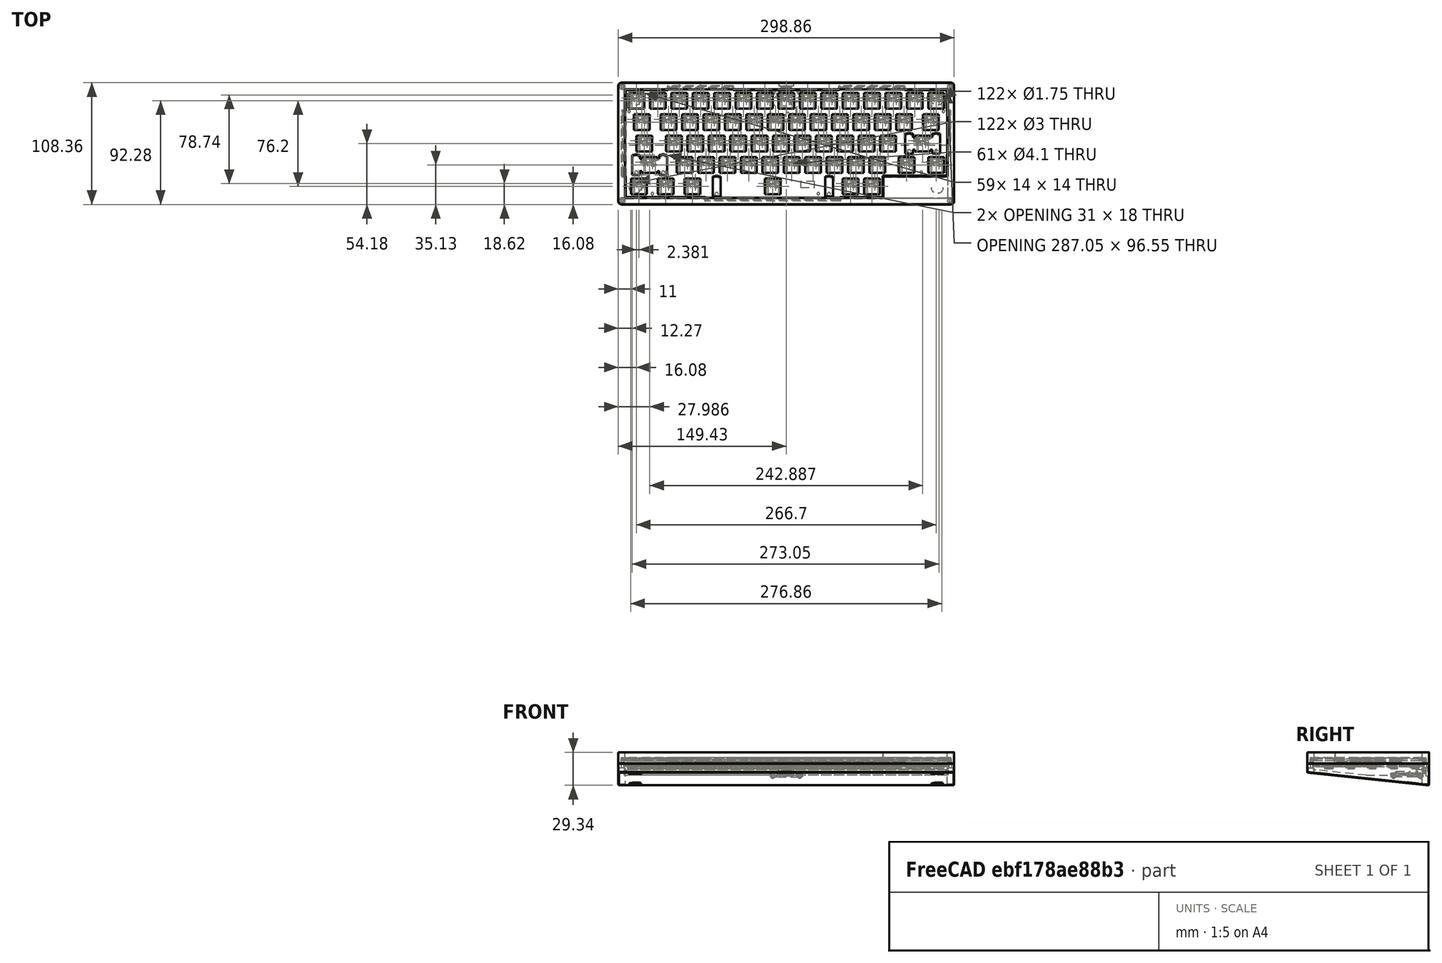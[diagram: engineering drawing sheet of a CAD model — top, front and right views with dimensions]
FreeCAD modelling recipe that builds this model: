
FCSTD DOCUMENT  (FreeCAD 0.20R29603 (Git))
Label: Five_Octave_Enclosure_v2
License: All rights reserved
LicenseURL: http://en.wikipedia.org/wiki/All_rights_reserved
objects: Sketcher::SketchObject×17, PartDesign::Pocket×9, TechDraw::DrawViewBalloon×8, PartDesign::Fillet×6, PartDesign::Pad×5, PartDesign::Body×4, Part::Feature×3, PartDesign::Hole×3, PartDesign::Chamfer×3, TechDraw::DrawSVGTemplate×2, TechDraw::DrawProjGroupItem×2, TechDraw::DrawProjGroup×2, TechDraw::DrawPage×2, Part::MultiFuse×1, App::DocumentObjectGroup×1, PartDesign::Boolean×1
note: 78 computed .brp shape members not serialized (recipe doc carries the construction recipe); baked Part::Feature solids carry a one-line shape summary decoded from their .brp

FEATURE [Part::Feature] Feature001  label="Five_Octave_Keys"
  Placement = pos=(0,0,-4.2) rot=(0,1,0;3.14159rad)
  shape: bbox 285.8 x 95.25 x 3.65 mm, 9961 faces, 246 solids (baked)
  expr: .Placement.Base.z = -0.8mm - 3.4mm
FEATURE [Part::Feature] Solid  label="Five_Octave_Plate"
  Placement = pos=(0,0,-0.8) rot=(0,0,1;0rad)
  shape: bbox 290.8 x 100.3 x 1.6 mm, 520 faces (baked)
FEATURE [Part::Feature] Feature  label="Five_Octave_MCU"
  shape: bbox 28.58 x 28.58 x 3.65 mm, 932 faces, 28 solids (baked)
FEATURE [Sketcher::SketchObject] Sketch
  AttachmentOffset = pos=(0,0,1.65) rot=(0,0,1;0rad)
  FullyConstrained = true
  MapMode = 5
  Placement = pos=(0,0,1.65) rot=(0,0,1;0rad)
  Support = -> [XY_Plane]
  expr: Constraints[12] = 15.637mm
  sketch-geometry (5):
    g0: LineSegment StartX=-4.47 StartY=15.637 StartZ=0 EndX=4.47 EndY=15.637 EndZ=0
    g1: LineSegment StartX=4.47 StartY=15.637 StartZ=0 EndX=4.47 EndY=8.337 EndZ=0
    g2: LineSegment StartX=4.47 StartY=8.337 StartZ=0 EndX=-4.47 EndY=8.337 EndZ=0
    g3: LineSegment StartX=-4.47 StartY=8.337 StartZ=0 EndX=-4.47 EndY=15.637 EndZ=0
    g4: GeomPoint X=0 Y=15.637 Z=0
  constraints (13):
    c: Coincident(g0,g1)
    c: Coincident(g1,g2)
    c: Coincident(g2,g3)
    c: Coincident(g3,g0)
    c: Horizontal(g0)
    c: Horizontal(g2)
    c: Vertical(g1)
    c: Vertical(g3)
    c: DistanceX(g0,g0) = 8.94
    c: DistanceY(g1,g1) = 7.3
    c: Symmetric(g0,g0,g4)
    c: PointOnObject(g4,g-2)
    c: DistanceY(g-1,g4) = 15.637
FEATURE [PartDesign::Pad] Pad
  Direction = (0,0,1)
  Length = 3.2
  Length2 = 10
  Profile = -> Sketch
  ReferenceAxis = -> Sketch [N_Axis]
  Type = 0
FEATURE [Sketcher::SketchObject] Sketch001
  ExternalGeometry = -> [Pad]
  FullyConstrained = true
  MapMode = 5
  Placement = pos=(0,15.637,0) rot=(0,0.707107,0.707107;3.14159rad)
  Support = -> [Pad]
  sketch-geometry (12):
    g0: ArcOfCircle CenterX=-3.22 CenterY=3.6 CenterZ=0 NormalX=0 NormalY=0 NormalZ=1 AngleXU=0 Radius=1.25 StartAngle=1.5708 EndAngle=3.14159
    g1: LineSegment StartX=-4.47 StartY=4.85 StartZ=0 EndX=-3.22 EndY=4.85 EndZ=0
    g2: LineSegment StartX=-4.47 StartY=3.6 StartZ=0 EndX=-4.47 EndY=4.85 EndZ=0
    g3: ArcOfCircle CenterX=3.22 CenterY=3.6 CenterZ=0 NormalX=0 NormalY=0 NormalZ=1 AngleXU=0 Radius=1.25 StartAngle=1e-16 EndAngle=1.5708
    g4: LineSegment StartX=3.22 StartY=4.85 StartZ=0 EndX=4.47 EndY=4.85 EndZ=0
    g5: LineSegment StartX=4.47 StartY=3.6 StartZ=0 EndX=4.47 EndY=4.85 EndZ=0
    g6: ArcOfCircle CenterX=-3.22 CenterY=2.9 CenterZ=0 NormalX=0 NormalY=0 NormalZ=1 AngleXU=0 Radius=1.25 StartAngle=3.14159 EndAngle=4.71239
    g7: LineSegment StartX=-4.47 StartY=1.65 StartZ=0 EndX=-4.47 EndY=2.9 EndZ=0
    g8: LineSegment StartX=-4.47 StartY=1.65 StartZ=0 EndX=-3.22 EndY=1.65 EndZ=0
    g9: ArcOfCircle CenterX=3.22 CenterY=2.9 CenterZ=0 NormalX=0 NormalY=0 NormalZ=1 AngleXU=0 Radius=1.25 StartAngle=4.71239 EndAngle=6.28319
    g10: LineSegment StartX=4.47 StartY=1.65 StartZ=0 EndX=3.22 EndY=1.65 EndZ=0
    g11: LineSegment StartX=4.47 StartY=1.65 StartZ=0 EndX=4.47 EndY=2.9 EndZ=0
  constraints (36):
    c: PointOnObject(g0,g-3)
    c: PointOnObject(g0,g-5)
    c: Radius(g0) = 1.25
    c: Coincident(g1,g-5)
    c: Coincident(g1,g0)
    c: DistanceX(g1,g1) = 1.25
    c: Coincident(g2,g0)
    c: Coincident(g2,g1)
    c: DistanceY(g2,g2) = 1.25
    c: PointOnObject(g3,g-3)
    c: PointOnObject(g3,g-6)
    c: Coincident(g4,g3)
    c: Coincident(g4,g-6)
    c: Coincident(g5,g4)
    c: Coincident(g5,g3)
    c: PointOnObject(g6,g-5)
    c: PointOnObject(g6,g-4)
    c: Equal(g6,g0)
    c: Equal(g3,g0)
    c: Equal(g1,g4)
    c: Equal(g5,g2)
    c: Coincident(g7,g-5)
    c: Coincident(g8,g7)
    c: Coincident(g8,g6)
    c: Coincident(g6,g7)
    c: Equal(g7,g2)
    c: Equal(g1,g8)
    c: PointOnObject(g9,g-6)
    c: PointOnObject(g9,g-4)
    c: Equal(g9,g0)
    c: Coincident(g10,g-6)
    c: Coincident(g11,g10)
    c: Coincident(g9,g11)
    c: Coincident(g10,g9)
    c: Equal(g10,g1)
    c: Equal(g11,g2)
FEATURE [PartDesign::Pocket] Pocket
  BaseFeature = -> Pad
  Direction = (0,-1,2e-16)
  Length = 7.3
  Length2 = 5
  Profile = -> Sketch001
  ReferenceAxis = -> Sketch001 [N_Axis]
  Type = 0
FEATURE [PartDesign::Body] Body  label="USB"
  Group = -> [Sketch,Pad,Sketch001,Pocket]
  Origin = -> Origin
  Tip = -> Pocket
FEATURE [Part::MultiFuse] Fusion  label="MCU"
  Placement = pos=(0,34.3875,-13.6) rot=(-1,0,0;0rad)
  Shapes = -> [Body,Feature]
  expr: .Placement.Base.y = 19.05mm * 2.5 - 28.575mm / 2 + 1.05mm
  expr: .Placement.Base.z = -0.8mm - 5mm - 7.8mm
FEATURE [App::DocumentObjectGroup] Group  label="External Components"
  Group = -> [Solid,Feature001,Fusion]
FEATURE [Sketcher::SketchObject] Sketch002
  AttachmentOffset = pos=(0,0,-3.2) rot=(0,0,1;0rad)
  FullyConstrained = true
  MapMode = 5
  Placement = pos=(0,0,-3.2) rot=(0,0,1;0rad)
  Support = -> [XY_Plane001]
  expr: .AttachmentOffset.Base.z = -2mm - 1.2mm
  expr: Constraints[10] = 19.05mm * 15 + (0.55mm + 6mm) * 2
  expr: Constraints[11] = 19.05mm * 5 + (0.55mm + 6mm) * 2
  sketch-geometry (5):
    g0: LineSegment StartX=149.425 StartY=-54.175 StartZ=0 EndX=149.425 EndY=54.175 EndZ=0
    g1: LineSegment StartX=149.425 StartY=54.175 StartZ=0 EndX=-149.425 EndY=54.175 EndZ=0
    g2: LineSegment StartX=-149.425 StartY=54.175 StartZ=0 EndX=-149.425 EndY=-54.175 EndZ=0
    g3: LineSegment StartX=-149.425 StartY=-54.175 StartZ=0 EndX=149.425 EndY=-54.175 EndZ=0
    g4: GeomPoint X=0 Y=0 Z=0
  constraints (12):
    c: Coincident(g0,g1)
    c: Coincident(g1,g2)
    c: Coincident(g2,g3)
    c: Coincident(g3,g0)
    c: Horizontal(g1)
    c: Horizontal(g3)
    c: Vertical(g0)
    c: Vertical(g2)
    c: Symmetric(g1,g0,g4)
    c: Coincident(g4,g-1)
    c: DistanceX(g1,g1) = 298.85
    c: DistanceY(g2,g2) = 108.35
FEATURE [PartDesign::Pad] Pad001  label="Pad001 - Base"
  Direction = (0,0,-1)
  Length = 20
  Length2 = 10
  Profile = -> Sketch002
  ReferenceAxis = -> Sketch002 [N_Axis]
  Type = 0
  UseCustomVector = true
FEATURE [Sketcher::SketchObject] Sketch003
  ExternalGeometry = -> [Pad001]
  FullyConstrained = true
  MapMode = 5
  Placement = pos=(149.425,0,0) rot=(0.57735,0.57735,0.57735;2.0944rad)
  Support = -> [Pad001]
  sketch-geometry (6):
    g0: LineSegment StartX=-54.175 StartY=-11.2 StartZ=0 EndX=54.175 EndY=-22.588 EndZ=0
    g1: LineSegment StartX=54.175 StartY=-22.588 StartZ=0 EndX=54.175 EndY=-23.2 EndZ=0
    g2: LineSegment StartX=54.175 StartY=-23.2 StartZ=0 EndX=-54.175 EndY=-23.2 EndZ=0
    g3: LineSegment StartX=-54.175 StartY=-23.2 StartZ=0 EndX=-54.175 EndY=-11.2 EndZ=0
    g4: LineSegment StartX=-54.175 StartY=-7.17797 StartZ=0 EndX=54.175 EndY=-18.566 EndZ=0
    g5: LineSegment StartX=-54.175 StartY=-11.2 StartZ=0 EndX=-53.7569 EndY=-7.22191 EndZ=0
  constraints (18):
    c: PointOnObject(g0,g-3)
    c: PointOnObject(g0,g-4)
    c: Coincident(g1,g0)
    c: Coincident(g1,g-4)
    c: Coincident(g2,g1)
    c: Coincident(g2,g-3)
    c: Coincident(g3,g2)
    c: Coincident(g3,g0)
    c: DistanceY(g0,g-4) = 19.388
    c: PointOnObject(g4,g-4)
    c: PointOnObject(g4,g-3)
    c: Angle(g0,g-1) = 0.10472
    c: Equal(g0,g4)
    c: Coincident(g5,g0)
    c: PointOnObject(g5,g4)
    c: Perpendicular(g5,g4)
    c: Distance(g5) = 4
    c: DistanceY(g0,g-3) = 8
FEATURE [PartDesign::Pocket] Pocket001  label="Pocket001 - Base angle"
  BaseFeature = -> Pad001
  Direction = (-1,0,0)
  Length = 300
  Length2 = 5
  Profile = -> Sketch003
  ReferenceAxis = -> Sketch003 [N_Axis]
  Type = 0
FEATURE [Sketcher::SketchObject] Sketch004
  FullyConstrained = true
  MapMode = 5
  Support = -> [XY_Plane002]
  expr: Constraints[10] = 19.05mm * 15 + (0.55mm + 6mm) * 2
  expr: Constraints[11] = 19.05mm * 5 + (0.55mm + 6mm) * 2
  expr: Constraints[29] = 19.05mm * 3
  sketch-geometry (11):
    g0: LineSegment StartX=149.425 StartY=-54.175 StartZ=0 EndX=149.425 EndY=54.175 EndZ=0
    g1: LineSegment StartX=149.425 StartY=54.175 StartZ=0 EndX=-149.425 EndY=54.175 EndZ=0
    g2: LineSegment StartX=-149.425 StartY=54.175 StartZ=0 EndX=-149.425 EndY=-54.175 EndZ=0
    g3: LineSegment StartX=-149.425 StartY=-54.175 StartZ=0 EndX=149.425 EndY=-54.175 EndZ=0
    g4: GeomPoint X=0 Y=0 Z=0
    g5: LineSegment StartX=-143.425 StartY=48.175 StartZ=0 EndX=-143.425 EndY=-48.175 EndZ=0
    g6: LineSegment StartX=-143.425 StartY=-48.175 StartZ=0 EndX=86.275 EndY=-48.175 EndZ=0
    g7: LineSegment StartX=86.275 StartY=-48.175 StartZ=0 EndX=86.275 EndY=-29.125 EndZ=0
    g8: LineSegment StartX=86.275 StartY=-29.125 StartZ=0 EndX=143.425 EndY=-29.125 EndZ=0
    g9: LineSegment StartX=143.425 StartY=-29.125 StartZ=0 EndX=143.425 EndY=48.175 EndZ=0
    g10: LineSegment StartX=143.425 StartY=48.175 StartZ=0 EndX=-143.425 EndY=48.175 EndZ=0
  constraints (32):
    c: Coincident(g0,g1)
    c: Coincident(g1,g2)
    c: Coincident(g2,g3)
    c: Coincident(g3,g0)
    c: Horizontal(g1)
    c: Horizontal(g3)
    c: Vertical(g0)
    c: Vertical(g2)
    c: Symmetric(g1,g0,g4)
    c: Coincident(g4,g-1)
    c: DistanceX(g1,g1) = 298.85
    c: DistanceY(g2,g2) = 108.35
    c: Vertical(g5)
    c: Coincident(g6,g5)
    c: Horizontal(g6)
    c: Coincident(g7,g6)
    c: Vertical(g7)
    c: Coincident(g8,g7)
    c: Horizontal(g8)
    c: Coincident(g9,g8)
    c: Vertical(g9)
    c: Coincident(g10,g9)
    c: Coincident(g10,g5)
    c: Horizontal(g10)
    c: DistanceY(g5,g1) = 6
    c: DistanceX(g9,g0) = 6
    c: DistanceX(g1,g5) = 6
    c: DistanceY(g2,g5) = 6
    c: DistanceY(g7,g7) = 19.05
    c: DistanceX(g8,g8) = 57.15
    c: DistanceX(g10,g10) = 286.85
    c: DistanceY(g5,g5) = 96.35
FEATURE [PartDesign::Pad] Pad002
  Direction = (0,0,1)
  Length = 6.8
  Length2 = 3.2
  Profile = -> Sketch004
  ReferenceAxis = -> Sketch004 [N_Axis]
  Type = 4
  expr: Length = 0.8mm + 6mm
FEATURE [Sketcher::SketchObject] Sketch006
  AttachmentOffset = pos=(0,0,-3.2) rot=(0,0,1;0rad)
  FullyConstrained = true
  MapMode = 5
  Placement = pos=(0,0,-3.2) rot=(0,0,1;0rad)
  Support = -> [XY_Plane003]
  expr: Constraints[10] = 19.05mm * 15 + 1mm * 2 + 0.05mm * 2
  expr: Constraints[11] = 19.05mm * 5 + 1mm * 2 + 0.05mm * 2
  sketch-geometry (5):
    g0: LineSegment StartX=-143.925 StartY=48.675 StartZ=0 EndX=-143.925 EndY=-48.675 EndZ=0
    g1: LineSegment StartX=-143.925 StartY=-48.675 StartZ=0 EndX=143.925 EndY=-48.675 EndZ=0
    g2: LineSegment StartX=143.925 StartY=-48.675 StartZ=0 EndX=143.925 EndY=48.675 EndZ=0
    g3: LineSegment StartX=143.925 StartY=48.675 StartZ=0 EndX=-143.925 EndY=48.675 EndZ=0
    g4: GeomPoint X=0 Y=0 Z=0
  constraints (12):
    c: Coincident(g0,g1)
    c: Coincident(g1,g2)
    c: Coincident(g2,g3)
    c: Coincident(g3,g0)
    c: Horizontal(g1)
    c: Horizontal(g3)
    c: Vertical(g0)
    c: Vertical(g2)
    c: Symmetric(g1,g0,g4)
    c: Coincident(g4,g-1)
    c: DistanceX(g3,g3) = 287.85
    c: DistanceY(g0,g0) = 97.35
FEATURE [PartDesign::Pad] Pad003
  Direction = (0,0,-1)
  Length = 20
  Length2 = 10
  Profile = -> Sketch006
  ReferenceAxis = -> Sketch006 [N_Axis]
  Type = 0
  UseCustomVector = true
FEATURE [Sketcher::SketchObject] Sketch007
  ExternalGeometry = -> [Pad003]
  FullyConstrained = true
  MapMode = 5
  Placement = pos=(143.925,0,0) rot=(0.57735,0.57735,0.57735;2.0944rad)
  Support = -> [Pad003]
  sketch-geometry (9):
    g0: LineSegment StartX=48.675 StartY=-18.8883 StartZ=0 EndX=-53.175 EndY=-8.18348 EndZ=0
    g1: LineSegment StartX=48.675 StartY=-13.6 StartZ=0 EndX=48.675 EndY=-23.2 EndZ=0
    g2: LineSegment StartX=48.675 StartY=-23.2 StartZ=0 EndX=-48.675 EndY=-23.2 EndZ=0
    g3: LineSegment StartX=-48.675 StartY=-23.2 StartZ=0 EndX=-48.675 EndY=-8.65644 EndZ=0
    g4: GeomPoint X=-53.175 Y=-11.2 Z=0
    g5: LineSegment StartX=-53.175 StartY=-11.2 StartZ=0 EndX=-52.8614 EndY=-8.21643 EndZ=0
    g6: LineSegment StartX=48.675 StartY=-13.6 StartZ=0 EndX=-48.675 EndY=-13.6 EndZ=0
    g7: LineSegment StartX=48.675 StartY=-13.6 StartZ=0 EndX=-1.64021 EndY=-13.6 EndZ=0
    g8: LineSegment StartX=-48.675 StartY=-8.65644 StartZ=0 EndX=-1.64021 EndY=-13.6 EndZ=0
  constraints (25):
    c: PointOnObject(g0,g-3)
    c: DistanceX(g0,g-4) = 4.5
    c: Angle(g0,g-1) = 0.10472
    c: Coincident(g1,g-3)
    c: Coincident(g2,g1)
    c: Coincident(g2,g-4)
    c: Vertical(g0,g4)
    c: Coincident(g5,g4)
    c: PointOnObject(g5,g0)
    c: Perpendicular(g5,g0)
    c: DistanceY(g4,g-4) = 8
    c: Distance(g5) = 3
    c: Coincident(g2,g3)
    c: PointOnObject(g6,g-3)
    c: PointOnObject(g6,g-4)
    c: Horizontal(g6)
    c: DistanceY(g6,g-1) = 13.6
    c: Coincident(g1,g6)
    c: Coincident(g7,g1)
    c: PointOnObject(g7,g0)
    c: PointOnObject(g7,g6)
    c: PointOnObject(g3,g-4)
    c: PointOnObject(g3,g0)
    c: Coincident(g8,g3)
    c: Coincident(g8,g7)
FEATURE [PartDesign::Pocket] Pocket002
  BaseFeature = -> Pad003
  Direction = (-1,0,0)
  Length = 300
  Length2 = 5
  Profile = -> Sketch007
  ReferenceAxis = -> Sketch007 [N_Axis]
  Type = 0
FEATURE [PartDesign::Body] Body003  label="Case pocket"
  Group = -> [Sketch006,Pad003,Sketch007,Pocket002]
  Origin = -> Origin003
  Tip = -> Pocket002
FEATURE [PartDesign::Boolean] Boolean  label="Boolean - Inner"
  BaseFeature = -> Pocket001
  Group = -> [Body003]
  Type = 1
FEATURE [PartDesign::Fillet] Fillet  label="Fillet - Inner radius"
  Base = -> Boolean [Edge20,Edge17,Edge23,Edge21]
  BaseFeature = -> Boolean
  Radius = 2
  SupportTransform = false
  UseAllEdges = false
FEATURE [Sketcher::SketchObject] Sketch008
  AttachmentOffset = pos=(0,0,-4) rot=(0,0,1;0rad)
  ExternalGeometry = -> [Fillet]
  FullyConstrained = true
  MapMode = 5
  Placement = pos=(0,0,-7.2) rot=(0,0,1;0rad)
  Support = -> [Fillet]
  sketch-geometry (4):
    g0: Circle CenterX=-145.925 CenterY=50.675 CenterZ=0 NormalX=0 NormalY=0 NormalZ=1 AngleXU=0 Radius=2.5
    g1: Circle CenterX=-145.925 CenterY=-50.675 CenterZ=0 NormalX=0 NormalY=0 NormalZ=1 AngleXU=0 Radius=2.5
    g2: Circle CenterX=145.925 CenterY=-50.675 CenterZ=0 NormalX=0 NormalY=0 NormalZ=1 AngleXU=0 Radius=2.5
    g3: Circle CenterX=145.925 CenterY=50.675 CenterZ=0 NormalX=0 NormalY=0 NormalZ=1 AngleXU=0 Radius=2.5
  constraints (12):
    c: Diameter(g0) = 5
    c: DistanceX(g-5,g0) = 3.5
    c: DistanceY(g0,g-5) = 3.5
    c: DistanceY(g-3,g1) = 3.5
    c: Equal(g1,g0)
    c: Equal(g2,g1)
    c: Vertical(g1,g0)
    c: Horizontal(g1,g2)
    c: DistanceX(g3,g-4) = 3.5
    c: Equal(g3,g0)
    c: Horizontal(g3,g0)
    c: Vertical(g3,g2)
FEATURE [PartDesign::Pocket] Pocket003  label="Pocket003 - Margin for screw to top frame"
  BaseFeature = -> Fillet
  Direction = (0,0,-1)
  Length = 30
  Length2 = 5
  Profile = -> Sketch008
  ReferenceAxis = -> Sketch008 [N_Axis]
  Type = 0
FEATURE [Sketcher::SketchObject] Sketch009
  ExternalGeometry = -> [Pocket003]
  FullyConstrained = true
  MapMode = 5
  Placement = pos=(0,0,-3.2) rot=(0,0,1;0rad)
  Support = -> [Pocket003]
  sketch-geometry (4):
    g0: Circle CenterX=-145.925 CenterY=50.675 CenterZ=0 NormalX=0 NormalY=0 NormalZ=1 AngleXU=0 Radius=1.1
    g1: Circle CenterX=-145.925 CenterY=-50.675 CenterZ=0 NormalX=0 NormalY=0 NormalZ=1 AngleXU=0 Radius=1.1
    g2: Circle CenterX=145.925 CenterY=50.675 CenterZ=0 NormalX=0 NormalY=0 NormalZ=1 AngleXU=0 Radius=1.1
    g3: Circle CenterX=145.925 CenterY=-50.675 CenterZ=0 NormalX=0 NormalY=0 NormalZ=1 AngleXU=0 Radius=1.1
  constraints (12):
    c: DistanceX(g-3,g0) = 3.5
    c: DistanceY(g0,g-3) = 3.5
    c: Diameter(g0) = 2.2
    c: Equal(g1,g0)
    c: Equal(g0,g2)
    c: Equal(g2,g3)
    c: Horizontal(g1,g3)
    c: Horizontal(g0,g2)
    c: Vertical(g1,g0)
    c: Vertical(g3,g2)
    c: DistanceX(g2,g-5) = 3.5
    c: DistanceY(g-4,g1) = 3.5
FEATURE [PartDesign::Hole] Hole  label="Hole - Through hole to top frame"
  BaseFeature = -> Pocket003
  CustomThreadClearance = 0
  Depth = 25
  DepthType = 0
  Diameter = 2.2
  DrillForDepth = false
  DrillPoint = 1
  DrillPointAngle = 118
  HoleCutCountersinkAngle = 90
  HoleCutCustomValues = false
  HoleCutDepth = 0
  HoleCutDiameter = 6.1
  HoleCutType = 0
  ModelThread = false
  Profile = -> Sketch009
  Tapered = false
  TaperedAngle = 90
  ThreadClass = 0
  ThreadDepth = 25
  ThreadDepthType = 0
  ThreadDirection = 0
  ThreadFit = 1
  ThreadSize = 0
  ThreadType = 0
  Threaded = false
  UseCustomThreadClearance = false
FEATURE [PartDesign::Fillet] Fillet001  label="Fillet001 - Outer"
  Base = -> Hole [Edge21,Edge19,Edge17,Edge22]
  BaseFeature = -> Hole
  Radius = 3
  SupportTransform = false
  UseAllEdges = false
FEATURE [PartDesign::Chamfer] Chamfer  label="Chamfer - Outer"
  Angle = 45
  Base = -> Fillet001 [Edge29]
  BaseFeature = -> Fillet001
  ChamferType = 0
  FlipDirection = false
  Size = 0.5
  Size2 = 1
  SupportTransform = false
  UseAllEdges = false
FEATURE [Sketcher::SketchObject] Sketch010
  ExternalGeometry = -> [Pad002]
  FullyConstrained = true
  MapMode = 5
  Placement = pos=(0,0,-3.2) rot=(1,0,0;3.14159rad)
  Support = -> [Pad002]
  sketch-geometry (4):
    g0: Circle CenterX=-145.925 CenterY=50.675 CenterZ=0 NormalX=0 NormalY=0 NormalZ=1 AngleXU=0 Radius=0.8
    g1: Circle CenterX=-145.925 CenterY=-50.675 CenterZ=0 NormalX=0 NormalY=0 NormalZ=1 AngleXU=0 Radius=0.8
    g2: Circle CenterX=145.925 CenterY=50.675 CenterZ=0 NormalX=0 NormalY=0 NormalZ=1 AngleXU=0 Radius=0.8
    g3: Circle CenterX=145.925 CenterY=-50.675 CenterZ=0 NormalX=0 NormalY=0 NormalZ=1 AngleXU=0 Radius=0.8
  constraints (12):
    c: Diameter(g0) = 1.6
    c: DistanceX(g-3,g0) = 3.5
    c: DistanceY(g0,g-3) = 3.5
    c: Equal(g0,g1)
    c: Equal(g1,g2)
    c: Equal(g3,g2)
    c: Vertical(g2,g3)
    c: Vertical(g0,g1)
    c: Horizontal(g0,g2)
    c: Horizontal(g1,g3)
    c: DistanceX(g2,g-6) = 3.5
    c: DistanceY(g-4,g1) = 3.5
FEATURE [PartDesign::Hole] Hole001  label="Hole001 - Screw to case"
  BaseFeature = -> Pad002
  CustomThreadClearance = 0
  Depth = 4.2
  DepthType = 0
  Diameter = 2.2
  DrillForDepth = false
  DrillPoint = 1
  DrillPointAngle = 118
  HoleCutCountersinkAngle = 90
  HoleCutCustomValues = false
  HoleCutDepth = 0
  HoleCutDiameter = 6.1
  HoleCutType = 0
  ModelThread = false
  Profile = -> Sketch010
  Tapered = false
  TaperedAngle = 90
  ThreadClass = 0
  ThreadDepth = 4.2
  ThreadDepthType = 0
  ThreadDirection = 0
  ThreadFit = 1
  ThreadSize = 6
  ThreadType = 1
  Threaded = false
  UseCustomThreadClearance = false
FEATURE [PartDesign::Fillet] Fillet003  label="Fillet003 - Outer"
  Base = -> Hole001 [Edge2,Edge1,Edge8,Edge5]
  BaseFeature = -> Hole001
  Radius = 3
  SupportTransform = false
  UseAllEdges = false
FEATURE [Sketcher::SketchObject] Sketch011
  ExternalGeometry = -> [Fillet003]
  FullyConstrained = true
  MapMode = 5
  Placement = pos=(0,0,-3.2) rot=(1,0,0;3.14159rad)
  Support = -> [Fillet003]
  expr: Constraints[12] = 19.05mm * 3 + 1.05mm * 2
  expr: Constraints[24] = 19.05mm * 6.25 + 1.05mm * 2
  expr: Constraints[36] = 19.05mm * (6.25 / 2 - 2.5)
  expr: Constraints[47] = 19.05mm * 3 + 1.05mm * 2
  expr: Constraints[49] = 19.05mm * 4
  expr: Constraints[64] = 19.05mm * 3 + 1.05mm * 2
  expr: Constraints[65] = 19.05mm * 4
  expr: Constraints[76] = 19.05mm * 2 + 1.05mm * 2
  expr: Constraints[81] = 19.05mm * 0.5
  sketch-geometry (31):
    g0: LineSegment StartX=-143.925 StartY=48.675 StartZ=0 EndX=-72.4875 EndY=48.675 EndZ=0
    g1: LineSegment StartX=-143.925 StartY=48.675 StartZ=0 EndX=-143.925 EndY=29.625 EndZ=0
    g2: LineSegment StartX=-143.925 StartY=29.625 StartZ=0 EndX=-146.425 EndY=29.625 EndZ=0
    g3: LineSegment StartX=-146.425 StartY=29.625 StartZ=0 EndX=-146.425 EndY=-29.625 EndZ=0
    g4: LineSegment StartX=-146.425 StartY=-29.625 StartZ=0 EndX=-143.925 EndY=-29.625 EndZ=0
    g5: GeomPoint X=-146.425 Y=0 Z=0
    g6: LineSegment StartX=-143.925 StartY=-29.625 StartZ=0 EndX=-143.925 EndY=-48.675 EndZ=0
    g7: LineSegment StartX=48.675 StartY=48.675 StartZ=0 EndX=48.675 EndY=51.175 EndZ=0
    g8: LineSegment StartX=48.675 StartY=51.175 StartZ=0 EndX=-72.4875 EndY=51.175 EndZ=0
    g9: LineSegment StartX=-72.4875 StartY=51.175 StartZ=0 EndX=-72.4875 EndY=48.675 EndZ=0
    g10: LineSegment StartX=48.675 StartY=48.675 StartZ=0 EndX=86.775 EndY=48.675 EndZ=0
    g11: LineSegment StartX=86.775 StartY=48.675 StartZ=0 EndX=86.775 EndY=29.625 EndZ=0
    g12: LineSegment StartX=86.775 StartY=29.625 StartZ=0 EndX=143.925 EndY=29.625 EndZ=0
    g13: GeomPoint X=-11.9062 Y=48.675 Z=0
    g14: LineSegment StartX=-143.925 StartY=-48.675 StartZ=0 EndX=-105.825 EndY=-48.675 EndZ=0
    g15: LineSegment StartX=-46.575 StartY=-48.675 StartZ=0 EndX=-46.575 EndY=-51.175 EndZ=0
    g16: LineSegment StartX=-46.575 StartY=-51.175 StartZ=0 EndX=-105.825 EndY=-51.175 EndZ=0
    g17: LineSegment StartX=-105.825 StartY=-51.175 StartZ=0 EndX=-105.825 EndY=-48.675 EndZ=0
    g18: GeomPoint X=-76.2 Y=-48.675 Z=0
    g19: LineSegment StartX=-46.575 StartY=-48.675 StartZ=0 EndX=46.575 EndY=-48.675 EndZ=0
    g20: LineSegment StartX=105.825 StartY=-48.675 StartZ=0 EndX=105.825 EndY=-51.175 EndZ=0
    g21: LineSegment StartX=105.825 StartY=-51.175 StartZ=0 EndX=46.575 EndY=-51.175 EndZ=0
    g22: LineSegment StartX=46.575 StartY=-51.175 StartZ=0 EndX=46.575 EndY=-48.675 EndZ=0
    g23: LineSegment StartX=105.825 StartY=-48.675 StartZ=0 EndX=143.925 EndY=-48.675 EndZ=0
    g24: GeomPoint X=76.2 Y=-48.675 Z=0
    g25: LineSegment StartX=143.925 StartY=29.625 StartZ=0 EndX=143.925 EndY=10.575 EndZ=0
    g26: LineSegment StartX=143.925 StartY=10.575 StartZ=0 EndX=146.425 EndY=10.575 EndZ=0
    g27: LineSegment StartX=146.425 StartY=10.575 StartZ=0 EndX=146.425 EndY=-29.625 EndZ=0
    g28: LineSegment StartX=146.425 StartY=-29.625 StartZ=0 EndX=143.925 EndY=-29.625 EndZ=0
    g29: LineSegment StartX=143.925 StartY=-48.675 StartZ=0 EndX=143.925 EndY=-29.625 EndZ=0
    g30: GeomPoint X=143.925 Y=-9.525 Z=0
  constraints (83):
    c: Horizontal(g0)
    c: Coincident(g1,g0)
    c: Vertical(g1)
    c: DistanceX(g0,g-3) = 0.5
    c: DistanceY(g-3,g0) = 0.5
    c: Coincident(g2,g3)
    c: Coincident(g3,g4)
    c: Horizontal(g2)
    c: Horizontal(g4)
    c: Vertical(g3)
    c: Coincident(g2,g1)
    c: DistanceX(g2,g2) = 2.5
    c: DistanceY(g3,g3) = 59.25
    c: Symmetric(g2,g3,g5)
    c: Horizontal(g5,g-1)
    c: Coincident(g6,g4)
    c: Vertical(g6)
    c: DistanceX(g6,g-4) = 0.5
    c: DistanceY(g6,g-4) = 0.5
    c: Coincident(g7,g8)
    c: Coincident(g8,g9)
    c: Horizontal(g8)
    c: Vertical(g7)
    c: Vertical(g9)
    c: DistanceX(g8,g8) = 121.162
    c: Coincident(g0,g9)
    c: Coincident(g10,g7)
    c: Horizontal(g10)
    c: Coincident(g11,g10)
    c: Vertical(g11)
    c: Coincident(g12,g11)
    c: Horizontal(g12)
    c: DistanceY(g9,g9) = 2.5
    c: DistanceX(g-5,g10) = 0.5
    c: DistanceY(g-6,g12) = 0.5
    c: DistanceX(g-6,g12) = 0.5
    c: DistanceX(g13,g-1) = 11.9062
    c: Symmetric(g0,g7,g13)
    c: DistanceY(g-5,g10) = 0.5
    c: Coincident(g14,g6)
    c: Horizontal(g14)
    c: Coincident(g15,g16)
    c: Coincident(g16,g17)
    c: Horizontal(g16)
    c: Vertical(g15)
    c: Vertical(g17)
    c: Coincident(g14,g17)
    c: DistanceX(g16,g16) = 59.25
    c: DistanceY(g17,g17) = 2.5
    c: DistanceX(g18,g-1) = 76.2
    c: Symmetric(g14,g15,g18)
    c: Coincident(g19,g15)
    c: Horizontal(g19)
    c: Coincident(g20,g21)
    c: Coincident(g21,g22)
    c: Horizontal(g21)
    c: Vertical(g20)
    c: Vertical(g22)
    c: Coincident(g23,g20)
    c: Horizontal(g23)
    c: DistanceX(g-7,g23) = 0.5
    c: DistanceY(g23,g-7) = 0.5
    c: DistanceY(g22,g22) = 2.5
    c: Coincident(g19,g22)
    c: DistanceX(g21,g21) = 59.25
    c: DistanceX(g-1,g24) = 76.2
    c: Symmetric(g19,g20,g24)
    c: DistanceY(g15,g15) = 2.5
    c: Coincident(g25,g12)
    c: Vertical(g25)
    c: Coincident(g26,g27)
    c: Coincident(g27,g28)
    c: Horizontal(g26)
    c: Horizontal(g28)
    c: Vertical(g27)
    c: Coincident(g26,g25)
    c: DistanceY(g27,g27) = 40.2
    c: DistanceX(g26,g26) = 2.5
    c: Coincident(g29,g23)
    c: Coincident(g29,g28)
    c: Vertical(g29)
    c: DistanceY(g30,g-1) = 9.525
    c: Symmetric(g25,g28,g30)
FEATURE [Sketcher::SketchObject] Sketch012
  ExternalGeometry = -> [Chamfer]
  FullyConstrained = true
  MapMode = 5
  Placement = pos=(0,0,-3.2) rot=(0,0,1;0rad)
  Support = -> [Chamfer]
  expr: Constraints[46] = 19.05mm * 4
  expr: Constraints[47] = 19.05mm * 3
  expr: Constraints[49] = 19.05mm * 4
  expr: Constraints[50] = 19.05mm * 3
  expr: Constraints[55] = 19.05mm * 3
  expr: Constraints[56] = 19.05mm * 2
  expr: Constraints[57] = 19.05mm * 0.5
  expr: Constraints[58] = 19.05mm * 6.25
  expr: Constraints[59] = 19.05mm * (6.25 / 2 - 2.5)
  sketch-geometry (25):
    g0: LineSegment StartX=-143.925 StartY=28.575 StartZ=0 EndX=-145.925 EndY=28.575 EndZ=0
    g1: LineSegment StartX=-145.925 StartY=28.575 StartZ=0 EndX=-145.925 EndY=-28.575 EndZ=0
    g2: LineSegment StartX=-145.925 StartY=-28.575 StartZ=0 EndX=-143.925 EndY=-28.575 EndZ=0
    g3: LineSegment StartX=-143.925 StartY=-28.575 StartZ=0 EndX=-143.925 EndY=28.575 EndZ=0
    g4: LineSegment StartX=-71.4375 StartY=-48.675 StartZ=0 EndX=47.625 EndY=-48.675 EndZ=0
    g5: LineSegment StartX=47.625 StartY=-48.675 StartZ=0 EndX=47.625 EndY=-50.675 EndZ=0
    g6: LineSegment StartX=47.625 StartY=-50.675 StartZ=0 EndX=-71.4375 EndY=-50.675 EndZ=0
    g7: LineSegment StartX=-71.4375 StartY=-50.675 StartZ=0 EndX=-71.4375 EndY=-48.675 EndZ=0
    g8: LineSegment StartX=143.925 StartY=28.575 StartZ=0 EndX=145.925 EndY=28.575 EndZ=0
    g9: LineSegment StartX=145.925 StartY=28.575 StartZ=0 EndX=145.925 EndY=-9.525 EndZ=0
    g10: LineSegment StartX=145.925 StartY=-9.525 StartZ=0 EndX=143.925 EndY=-9.525 EndZ=0
    g11: LineSegment StartX=143.925 StartY=-9.525 StartZ=0 EndX=143.925 EndY=28.575 EndZ=0
    g12: LineSegment StartX=-104.775 StartY=48.675 StartZ=0 EndX=-47.625 EndY=48.675 EndZ=0
    g13: LineSegment StartX=-47.625 StartY=48.675 StartZ=0 EndX=-47.625 EndY=50.675 EndZ=0
    g14: LineSegment StartX=-47.625 StartY=50.675 StartZ=0 EndX=-104.775 EndY=50.675 EndZ=0
    g15: LineSegment StartX=-104.775 StartY=50.675 StartZ=0 EndX=-104.775 EndY=48.675 EndZ=0
    g16: LineSegment StartX=47.625 StartY=48.675 StartZ=0 EndX=104.775 EndY=48.675 EndZ=0
    g17: LineSegment StartX=104.775 StartY=48.675 StartZ=0 EndX=104.775 EndY=50.675 EndZ=0
    g18: LineSegment StartX=104.775 StartY=50.675 StartZ=0 EndX=47.625 EndY=50.675 EndZ=0
    g19: LineSegment StartX=47.625 StartY=50.675 StartZ=0 EndX=47.625 EndY=48.675 EndZ=0
    g20: GeomPoint X=-76.2 Y=50.675 Z=0
    g21: GeomPoint X=76.2 Y=50.675 Z=0
    g22: GeomPoint X=-145.925 Y=0 Z=0
    g23: GeomPoint X=-11.9062 Y=-50.675 Z=0
    g24: GeomPoint X=145.925 Y=9.525 Z=0
  constraints (65):
    c: Coincident(g0,g1)
    c: Coincident(g1,g2)
    c: Coincident(g2,g3)
    c: Coincident(g3,g0)
    c: Horizontal(g0)
    c: Horizontal(g2)
    c: Vertical(g1)
    c: Vertical(g3)
    c: Coincident(g4,g5)
    c: Coincident(g5,g6)
    c: Coincident(g6,g7)
    c: Coincident(g7,g4)
    c: Horizontal(g4)
    c: Horizontal(g6)
    c: Vertical(g5)
    c: Vertical(g7)
    c: Coincident(g8,g9)
    c: Coincident(g9,g10)
    c: Coincident(g10,g11)
    c: Coincident(g11,g8)
    c: Horizontal(g8)
    c: Horizontal(g10)
    c: Vertical(g9)
    c: Vertical(g11)
    c: Coincident(g12,g13)
    c: Coincident(g13,g14)
    c: Coincident(g14,g15)
    c: Coincident(g15,g12)
    c: Horizontal(g12)
    c: Horizontal(g14)
    c: Vertical(g13)
    c: Vertical(g15)
    c: Coincident(g16,g17)
    c: Coincident(g17,g18)
    c: Coincident(g18,g19)
    c: Coincident(g19,g16)
    c: Horizontal(g16)
    c: Horizontal(g18)
    c: Vertical(g17)
    c: Vertical(g19)
    c: DistanceY(g15,g15) = 2
    c: DistanceY(g19,g19) = 2
    c: DistanceY(g7,g7) = 2
    c: DistanceX(g0,g0) = 2
    c: DistanceX(g8,g8) = 2
    c: Symmetric(g14,g13,g20)
    c: DistanceX(g20,g-1) = 76.2
    c: DistanceX(g14,g14) = 57.15
    c: Symmetric(g18,g17,g21)
    c: DistanceX(g-1,g21) = 76.2
    c: DistanceX(g18,g18) = 57.15
    c: Symmetric(g0,g1,g22)
    c: Symmetric(g6,g5,g23)
    c: Symmetric(g8,g9,g24)
    c: Horizontal(g22,g-1)
    c: DistanceY(g1,g1) = 57.15
    c: DistanceY(g9,g9) = 38.1
    c: DistanceY(g-1,g24) = 9.525
    c: DistanceX(g6,g6) = 119.062
    c: DistanceX(g23,g-1) = 11.9062
    c: PointOnObject(g0,g-3)
    c: PointOnObject(g12,g-4)
    c: PointOnObject(g16,g-4)
    c: PointOnObject(g8,g-6)
    c: PointOnObject(g4,g-5)
FEATURE [PartDesign::Pad] Pad004  label="Pad004 - Poron base"
  BaseFeature = -> Chamfer
  Direction = (0,0,1)
  Length = 1.2
  Length2 = 10
  Profile = -> Sketch012
  ReferenceAxis = -> Sketch012 [N_Axis]
  Type = 0
FEATURE [PartDesign::Fillet] Fillet004  label="Fillet004 - Poron base"
  Base = -> Pad004 [Edge85,Edge83,Edge130,Edge128,Edge123,Edge121,Edge110,Edge107,Edge97,Edge94]
  BaseFeature = -> Pad004
  Radius = 1
  SupportTransform = false
  UseAllEdges = false
FEATURE [PartDesign::Pocket] Pocket004  label="Pocket004 - Poron margin"
  BaseFeature = -> Fillet003
  Direction = (0,0,1)
  Length = 5.2
  Length2 = 5
  Profile = -> Sketch011
  ReferenceAxis = -> Sketch011 [N_Axis]
  Type = 0
FEATURE [PartDesign::Fillet] Fillet005  label="Fillet005 - Inner radius"
  Base = -> Pocket004 [Edge90,Edge86,Edge92,Edge96,Edge100,Edge102,Edge108,Edge110,Edge114,Edge65,Edge68,Edge72,Edge78,Edge76,Edge82]
  BaseFeature = -> Pocket004
  Radius = 1
  SupportTransform = false
  UseAllEdges = false
FEATURE [Sketcher::SketchObject] Sketch013
  ExternalGeometry = -> [Fillet004]
  FullyConstrained = true
  MapMode = 5
  Placement = pos=(0,-5e-16,-13.6) rot=(0,0,1;0rad)
  Support = -> [Fillet004]
  expr: Constraints[11] = 19.05mm * 1.5
  expr: Constraints[12] = 19.05mm * 1.5
  sketch-geometry (26):
    g0: LineSegment StartX=14.2875 StartY=20.1 StartZ=0 EndX=14.2875 EndY=48.675 EndZ=0
    g1: LineSegment StartX=14.2875 StartY=48.675 StartZ=0 EndX=-14.2875 EndY=48.675 EndZ=0
    g2: LineSegment StartX=-14.2875 StartY=48.675 StartZ=0 EndX=-14.2875 EndY=20.1 EndZ=0
    g3: LineSegment StartX=-14.2875 StartY=20.1 StartZ=0 EndX=14.2875 EndY=20.1 EndZ=0
    g4: GeomPoint X=0 Y=34.3875 Z=0
    g5: LineSegment StartX=12 StartY=22.3875 StartZ=0 EndX=12 EndY=46.3875 EndZ=0
    g6: LineSegment StartX=12 StartY=46.3875 StartZ=0 EndX=-12 EndY=46.3875 EndZ=0
    g7: LineSegment StartX=-12 StartY=46.3875 StartZ=0 EndX=-12 EndY=22.3875 EndZ=0
    g8: LineSegment StartX=-12 StartY=22.3875 StartZ=0 EndX=12 EndY=22.3875 EndZ=0
    g9: GeomPoint X=0 Y=34.3875 Z=0
    g10: ArcOfCircle CenterX=-12 CenterY=46.3875 CenterZ=0 NormalX=0 NormalY=0 NormalZ=1 AngleXU=0 Radius=2.5 StartAngle=4.71239 EndAngle=6.28319
    g11: ArcOfCircle CenterX=-12 CenterY=22.3875 CenterZ=0 NormalX=0 NormalY=0 NormalZ=1 AngleXU=0 Radius=2.5 StartAngle=1e-16 EndAngle=1.5708
    g12: ArcOfCircle CenterX=12 CenterY=22.3875 CenterZ=0 NormalX=0 NormalY=0 NormalZ=1 AngleXU=0 Radius=2.5 StartAngle=1.5708 EndAngle=3.14159
    g13: ArcOfCircle CenterX=12 CenterY=46.3875 CenterZ=0 NormalX=0 NormalY=0 NormalZ=1 AngleXU=0 Radius=2.5 StartAngle=3.14159 EndAngle=4.71239
    g14: LineSegment StartX=-9.5 StartY=46.3875 StartZ=0 EndX=-9.5 EndY=48.675 EndZ=0
    g15: LineSegment StartX=9.5 StartY=46.3875 StartZ=0 EndX=9.5 EndY=48.675 EndZ=0
    g16: LineSegment StartX=-9.5 StartY=48.675 StartZ=0 EndX=9.5 EndY=48.675 EndZ=0
    g17: LineSegment StartX=-12 StartY=43.8875 StartZ=0 EndX=-14.2875 EndY=43.8875 EndZ=0
    g18: LineSegment StartX=-12 StartY=24.8875 StartZ=0 EndX=-14.2875 EndY=24.8875 EndZ=0
    g19: LineSegment StartX=-9.5 StartY=22.3875 StartZ=0 EndX=-9.5 EndY=20.1 EndZ=0
    g20: LineSegment StartX=9.5 StartY=22.3875 StartZ=0 EndX=9.5 EndY=20.1 EndZ=0
    g21: LineSegment StartX=12 StartY=24.8875 StartZ=0 EndX=14.2875 EndY=24.8875 EndZ=0
    g22: LineSegment StartX=12 StartY=43.8875 StartZ=0 EndX=14.2875 EndY=43.8875 EndZ=0
    g23: LineSegment StartX=14.2875 StartY=43.8875 StartZ=0 EndX=14.2875 EndY=24.8875 EndZ=0
    g24: LineSegment StartX=-14.2875 StartY=43.8875 StartZ=0 EndX=-14.2875 EndY=24.8875 EndZ=0
    g25: LineSegment StartX=-9.5 StartY=20.1 StartZ=0 EndX=9.5 EndY=20.1 EndZ=0
  constraints (73):
    c: Coincident(g0,g1)
    c: Coincident(g1,g2)
    c: Coincident(g2,g3)
    c: Coincident(g3,g0)
    c: Horizontal(g1)
    c: Horizontal(g3)
    c: Vertical(g0)
    c: Vertical(g2)
    c: Symmetric(g1,g0,g4)
    c: PointOnObject(g4,g-2)
    c: PointOnObject(g1,g-3)
    c: DistanceY(g2,g2) = 28.575
    c: DistanceX(g3,g3) = 28.575
    c: Coincident(g5,g6)
    c: Coincident(g6,g7)
    c: Coincident(g7,g8)
    c: Coincident(g8,g5)
    c: Horizontal(g6)
    c: Horizontal(g8)
    c: Vertical(g5)
    c: Vertical(g7)
    c: Symmetric(g6,g5,g9)
    c: Coincident(g9,g4)
    c: DistanceX(g6,g6) = 24
    c: DistanceY(g7,g7) = 24
    c: Coincident(g10,g6)
    c: PointOnObject(g10,g7)
    c: PointOnObject(g10,g6)
    c: Radius(g10) = 2.5
    c: Coincident(g11,g7)
    c: PointOnObject(g11,g7)
    c: PointOnObject(g11,g8)
    c: Coincident(g12,g5)
    c: PointOnObject(g12,g5)
    c: PointOnObject(g12,g8)
    c: Coincident(g13,g5)
    c: PointOnObject(g13,g6)
    c: PointOnObject(g13,g5)
    c: Equal(g10,g11)
    c: Equal(g10,g13)
    c: Equal(g12,g10)
    c: Coincident(g14,g10)
    c: PointOnObject(g14,g1)
    c: Vertical(g14)
    c: Coincident(g15,g13)
    c: PointOnObject(g15,g1)
    c: Vertical(g15)
    c: Coincident(g16,g14)
    c: Coincident(g16,g15)
    c: Coincident(g17,g10)
    c: PointOnObject(g17,g2)
    c: Horizontal(g17)
    c: Coincident(g18,g11)
    c: PointOnObject(g18,g2)
    c: Horizontal(g18)
    c: Coincident(g19,g11)
    c: PointOnObject(g19,g3)
    c: Vertical(g19)
    c: Coincident(g20,g12)
    c: PointOnObject(g20,g3)
    c: Vertical(g20)
    c: Coincident(g21,g12)
    c: PointOnObject(g21,g0)
    c: Horizontal(g21)
    c: Coincident(g22,g13)
    c: PointOnObject(g22,g0)
    c: Horizontal(g22)
    c: Coincident(g23,g22)
    c: Coincident(g21,g23)
    c: Coincident(g24,g17)
    c: Coincident(g25,g19)
    c: Coincident(g20,g25)
    c: Coincident(g24,g18)
FEATURE [PartDesign::Pocket] Pocket005  label="Pocket005 - MCU margin"
  BaseFeature = -> Fillet004
  Direction = (0,0,-1)
  Length = 1.6
  Length2 = 5
  Profile = -> Sketch013
  ReferenceAxis = -> Sketch013 [N_Axis]
  Type = 0
FEATURE [PartDesign::Fillet] Fillet006  label="Fillet006 - MCU margin"
  Base = -> Pocket005 [Edge205,Edge203,Edge211,Edge213,Edge219,Edge221,Edge175,Edge174]
  BaseFeature = -> Pocket005
  Radius = 2
  SupportTransform = false
  UseAllEdges = false
FEATURE [Sketcher::SketchObject] Sketch014
  ExternalGeometry = -> [Fillet006]
  FullyConstrained = true
  MapMode = 5
  Placement = pos=(0,-5e-16,-13.6) rot=(0,0,1;0rad)
  Support = -> [Fillet006]
  expr: Constraints[11] = 19.05mm * 1.5
  expr: Constraints[12] = 19.05mm * 1.5
  sketch-geometry (14):
    g0: LineSegment StartX=14.2875 StartY=20.1 StartZ=0 EndX=14.2875 EndY=48.675 EndZ=0
    g1: LineSegment StartX=14.2875 StartY=48.675 StartZ=0 EndX=-14.2875 EndY=48.675 EndZ=0
    g2: LineSegment StartX=-14.2875 StartY=48.675 StartZ=0 EndX=-14.2875 EndY=20.1 EndZ=0
    g3: LineSegment StartX=-14.2875 StartY=20.1 StartZ=0 EndX=14.2875 EndY=20.1 EndZ=0
    g4: GeomPoint X=0 Y=34.3875 Z=0
    g5: LineSegment StartX=12 StartY=22.3875 StartZ=0 EndX=12 EndY=46.3875 EndZ=0
    g6: LineSegment StartX=12 StartY=46.3875 StartZ=0 EndX=-12 EndY=46.3875 EndZ=0
    g7: LineSegment StartX=-12 StartY=46.3875 StartZ=0 EndX=-12 EndY=22.3875 EndZ=0
    g8: LineSegment StartX=-12 StartY=22.3875 StartZ=0 EndX=12 EndY=22.3875 EndZ=0
    g9: GeomPoint X=0 Y=34.3875 Z=0
    g10: Circle CenterX=-12 CenterY=46.3875 CenterZ=0 NormalX=0 NormalY=0 NormalZ=1 AngleXU=0 Radius=0.8
    g11: Circle CenterX=12 CenterY=46.3875 CenterZ=0 NormalX=0 NormalY=0 NormalZ=1 AngleXU=0 Radius=0.8
    g12: Circle CenterX=-12 CenterY=22.3875 CenterZ=0 NormalX=0 NormalY=0 NormalZ=1 AngleXU=0 Radius=0.8
    g13: Circle CenterX=12 CenterY=22.3875 CenterZ=0 NormalX=0 NormalY=0 NormalZ=1 AngleXU=0 Radius=0.8
  constraints (33):
    c: Coincident(g0,g1)
    c: Coincident(g1,g2)
    c: Coincident(g2,g3)
    c: Coincident(g3,g0)
    c: Horizontal(g1)
    c: Horizontal(g3)
    c: Vertical(g0)
    c: Vertical(g2)
    c: Symmetric(g1,g0,g4)
    c: PointOnObject(g4,g-2)
    c: Horizontal(g1,g-3)
    c: DistanceX(g1,g1) = 28.575
    c: DistanceY(g2,g2) = 28.575
    c: Coincident(g5,g6)
    c: Coincident(g6,g7)
    c: Coincident(g7,g8)
    c: Coincident(g8,g5)
    c: Horizontal(g6)
    c: Horizontal(g8)
    c: Vertical(g5)
    c: Vertical(g7)
    c: Symmetric(g6,g5,g9)
    c: Coincident(g9,g4)
    c: DistanceX(g6,g6) = 24
    c: DistanceY(g7,g7) = 24
    c: Coincident(g10,g6)
    c: Diameter(g10) = 1.6
    c: Coincident(g11,g5)
    c: Coincident(g12,g7)
    c: Coincident(g13,g5)
    c: Equal(g12,g13)
    c: Equal(g12,g10)
    c: Equal(g11,g10)
FEATURE [PartDesign::Hole] Hole002  label="Hole002 - Screw to MCU"
  BaseFeature = -> Fillet006
  CustomThreadClearance = 0
  Depth = 2.6
  DepthType = 0
  Diameter = 2.2
  DrillForDepth = false
  DrillPoint = 1
  DrillPointAngle = 118
  HoleCutCountersinkAngle = 90
  HoleCutCustomValues = false
  HoleCutDepth = 0
  HoleCutDiameter = 6.1
  HoleCutType = 0
  ModelThread = false
  Profile = -> Sketch014
  Tapered = false
  TaperedAngle = 90
  ThreadClass = 0
  ThreadDepth = 2.6
  ThreadDepthType = 0
  ThreadDirection = 0
  ThreadFit = 1
  ThreadSize = 6
  ThreadType = 1
  Threaded = false
  UseCustomThreadClearance = false
FEATURE [Sketcher::SketchObject] Sketch015
  ExternalGeometry = -> [Hole002]
  FullyConstrained = true
  MapMode = 5
  Placement = pos=(0,48.675,0) rot=(1,0,0;1.5708rad)
  Support = -> [Hole002]
  sketch-geometry (13):
    g0: LineSegment StartX=4.545 StartY=-10.725 StartZ=0 EndX=4.545 EndY=-9.975 EndZ=0
    g1: LineSegment StartX=3.245 StartY=-8.675 StartZ=0 EndX=-3.245 EndY=-8.675 EndZ=0
    g2: LineSegment StartX=-4.545 StartY=-9.975 StartZ=0 EndX=-4.545 EndY=-10.725 EndZ=0
    g3: LineSegment StartX=-3.245 StartY=-12.025 StartZ=0 EndX=3.245 EndY=-12.025 EndZ=0
    g4: GeomPoint X=0 Y=-10.35 Z=0
    g5: ArcOfCircle CenterX=-3.245 CenterY=-9.975 CenterZ=0 NormalX=0 NormalY=0 NormalZ=1 AngleXU=0 Radius=1.3 StartAngle=1.5708 EndAngle=3.14159
    g6: GeomPoint X=-4.545 Y=-8.675 Z=0
    g7: ArcOfCircle CenterX=-3.245 CenterY=-10.725 CenterZ=0 NormalX=0 NormalY=0 NormalZ=1 AngleXU=0 Radius=1.3 StartAngle=3.14159 EndAngle=4.71239
    g8: GeomPoint X=-4.545 Y=-12.025 Z=0
    g9: ArcOfCircle CenterX=3.245 CenterY=-10.725 CenterZ=0 NormalX=0 NormalY=0 NormalZ=1 AngleXU=0 Radius=1.3 StartAngle=4.71239 EndAngle=6.28319
    g10: GeomPoint X=4.545 Y=-12.025 Z=0
    g11: ArcOfCircle CenterX=3.245 CenterY=-9.975 CenterZ=0 NormalX=0 NormalY=0 NormalZ=1 AngleXU=0 Radius=1.3 StartAngle=1.82384e-11 EndAngle=1.5708
    g12: GeomPoint X=4.545 Y=-8.675 Z=0
  constraints (29):
    c: Horizontal(g1)
    c: Horizontal(g3)
    c: Vertical(g0)
    c: Vertical(g2)
    c: Symmetric(g6,g10,g4)
    c: PointOnObject(g4,g-2)
    c: DistanceY(g-3,g4) = 3.25
    c: DistanceY(g8,g6) = 3.35
    c: DistanceX(g6,g12) = 9.09
    c: PointOnObject(g6,g2)
    c: PointOnObject(g6,g1)
    c: Tangent(g2,g5) = -1.5708
    c: Tangent(g1,g5) = -1.5708
    c: PointOnObject(g8,g3)
    c: PointOnObject(g8,g2)
    c: Tangent(g3,g7) = -1.5708
    c: Tangent(g2,g7) = -1.5708
    c: PointOnObject(g10,g3)
    c: PointOnObject(g10,g0)
    c: Tangent(g3,g9) = -1.5708
    c: Tangent(g0,g9) = -1.5708
    c: PointOnObject(g12,g0)
    c: PointOnObject(g12,g1)
    c: Tangent(g0,g11) = -1.5708
    c: Tangent(g1,g11) = -1.5708
    c: Radius(g5) = 1.3
    c: Equal(g5,g7)
    c: Equal(g7,g9)
    c: Equal(g11,g5)
FEATURE [PartDesign::Pocket] Pocket006  label="Pocket006 - USB"
  BaseFeature = -> Hole002
  Direction = (0,1,-2e-16)
  Length = 6
  Length2 = 5
  Profile = -> Sketch015
  ReferenceAxis = -> Sketch015 [N_Axis]
  Type = 0
FEATURE [Sketcher::SketchObject] Sketch016
  ExternalGeometry = -> [Pocket006]
  FullyConstrained = true
  MapMode = 5
  Placement = pos=(0,54.175,0) rot=(0,0.707107,0.707107;3.14159rad)
  Support = -> [Pocket006]
  sketch-geometry (14):
    g0: GeomPoint X=-1.01188e-11 Y=-10.35 Z=0
    g1: LineSegment StartX=6.5 StartY=-12.35 StartZ=0 EndX=6.5 EndY=-8.35 EndZ=0
    g2: LineSegment StartX=4.5 StartY=-6.35 StartZ=0 EndX=-4.5 EndY=-6.35 EndZ=0
    g3: LineSegment StartX=-6.5 StartY=-8.35 StartZ=0 EndX=-6.5 EndY=-12.35 EndZ=0
    g4: LineSegment StartX=-4.5 StartY=-14.35 StartZ=0 EndX=4.5 EndY=-14.35 EndZ=0
    g5: GeomPoint X=-1.01188e-11 Y=-10.35 Z=0
    g6: ArcOfCircle CenterX=-4.5 CenterY=-8.35 CenterZ=0 NormalX=0 NormalY=0 NormalZ=1 AngleXU=0 Radius=2 StartAngle=1.5708 EndAngle=3.14159
    g7: GeomPoint X=-6.5 Y=-6.35 Z=0
    g8: ArcOfCircle CenterX=-4.5 CenterY=-12.35 CenterZ=0 NormalX=0 NormalY=0 NormalZ=1 AngleXU=0 Radius=2 StartAngle=3.14159 EndAngle=4.71239
    g9: GeomPoint X=-6.5 Y=-14.35 Z=0
    g10: ArcOfCircle CenterX=4.5 CenterY=-12.35 CenterZ=0 NormalX=0 NormalY=0 NormalZ=1 AngleXU=0 Radius=2 StartAngle=4.71239 EndAngle=6.28319
    g11: GeomPoint X=6.5 Y=-14.35 Z=0
    g12: ArcOfCircle CenterX=4.5 CenterY=-8.35 CenterZ=0 NormalX=0 NormalY=0 NormalZ=1 AngleXU=0 Radius=2 StartAngle=0 EndAngle=1.5708
    g13: GeomPoint X=6.5 Y=-6.35 Z=0
  constraints (29):
    c: Symmetric(g-3,g-4,g0)
    c: Horizontal(g2)
    c: Horizontal(g4)
    c: Vertical(g1)
    c: Vertical(g3)
    c: Symmetric(g7,g11,g5)
    c: Coincident(g0,g5)
    c: DistanceX(g7,g13) = 13
    c: DistanceY(g9,g7) = 8
    c: PointOnObject(g7,g2)
    c: PointOnObject(g7,g3)
    c: Tangent(g2,g6) = -1.5708
    c: Tangent(g3,g6) = -1.5708
    c: PointOnObject(g9,g3)
    c: PointOnObject(g9,g4)
    c: Tangent(g3,g8) = -1.5708
    c: Tangent(g4,g8) = -1.5708
    c: PointOnObject(g11,g4)
    c: PointOnObject(g11,g1)
    c: Tangent(g4,g10) = -1.5708
    c: Tangent(g1,g10) = -1.5708
    c: PointOnObject(g13,g2)
    c: PointOnObject(g13,g1)
    c: Tangent(g2,g12) = -1.5708
    c: Tangent(g1,g12) = -1.5708
    c: Radius(g6) = 2
    c: Equal(g6,g8)
    c: Equal(g6,g12)
    c: Equal(g12,g10)
FEATURE [PartDesign::Pocket] Pocket007  label="Pocket007 - USB margin"
  BaseFeature = -> Pocket006
  Direction = (0,-1,2e-16)
  Length = 3
  Length2 = 5
  Profile = -> Sketch016
  ReferenceAxis = -> Sketch016 [N_Axis]
  Type = 0
FEATURE [Sketcher::SketchObject] Sketch017
  ExternalGeometry = -> [Pocket007]
  FullyConstrained = true
  MapMode = 5
  Placement = pos=(0,-1.75623,-16.7094) rot=(1,0,0;3.03687rad)
  Support = -> [Pocket007]
  sketch-geometry (4):
    g0: Circle CenterX=-134.425 CenterY=37.7598 CenterZ=0 NormalX=0 NormalY=0 NormalZ=1 AngleXU=0 Radius=5.2
    g1: Circle CenterX=-134.425 CenterY=-41.1871 CenterZ=0 NormalX=0 NormalY=0 NormalZ=1 AngleXU=0 Radius=5.2
    g2: Circle CenterX=134.425 CenterY=-41.1871 CenterZ=0 NormalX=0 NormalY=0 NormalZ=1 AngleXU=0 Radius=5.2
    g3: Circle CenterX=134.425 CenterY=37.7598 CenterZ=0 NormalX=0 NormalY=0 NormalZ=1 AngleXU=0 Radius=5.2
  constraints (12):
    c: Diameter(g0) = 10.4
    c: Equal(g0,g2)
    c: Equal(g2,g3)
    c: Equal(g1,g3)
    c: Vertical(g0,g1)
    c: Vertical(g2,g3)
    c: Horizontal(g3,g0)
    c: Horizontal(g2,g1)
    c: DistanceX(g-4,g0) = 15
    c: DistanceX(g3,g-6) = 15
    c: DistanceY(g-5,g1) = 15
    c: DistanceY(g0,g-3) = 15
FEATURE [PartDesign::Pocket] Pocket008  label="Pocket008 - Foot"
  BaseFeature = -> Pocket007
  Direction = (0,0.104528,0.994522)
  Length = 1
  Length2 = 5
  Profile = -> Sketch017
  ReferenceAxis = -> Sketch017 [N_Axis]
  Type = 0
FEATURE [PartDesign::Chamfer] Chamfer002  label="Chamfer002 - Finish thread"
  Angle = 45
  Base = -> Pocket008 [Edge176,Edge266,Edge157,Edge166,Edge164,Edge163,Edge165,Face97,Face95,Face94,Face99,Face100]
  BaseFeature = -> Pocket008
  ChamferType = 0
  FlipDirection = false
  Size = 0.1
  Size2 = 1
  SupportTransform = false
  UseAllEdges = false
FEATURE [PartDesign::Body] Body001  label="Case"
  Group = -> [Sketch002,Pad001,Sketch003,Pocket001,Boolean,Fillet,Sketch008,Pocket003,Sketch009,Hole,Fillet001,Chamfer,Sketch012,Pad004,Fillet004,Sketch013,Pocket005,Fillet006,Sketch014,Hole002,Sketch015,Pocket006,Sketch016,Pocket007,Sketch017,Pocket008,Chamfer002]
  Origin = -> Origin001
  Tip = -> Chamfer002
FEATURE [PartDesign::Chamfer] Chamfer003  label="Chamfer003 - Finish thread"
  Angle = 45
  Base = -> Fillet005 [Edge19,Edge25,Edge35,Edge41,Edge32,Edge30,Edge4,Edge3,Edge55,Edge87,Edge113,Edge81,Edge20,Edge14,Edge101,Edge69,Edge67,Edge123,Edge125,Edge111,Edge91,Edge17,Edge163,Edge162,Edge183,Edge161,Edge164,Edge165,Edge160,Edge47,Edge140,Edge170,Edge169,Edge168,Edge167,Edge171,Edge166]
  BaseFeature = -> Fillet005
  ChamferType = 0
  FlipDirection = false
  Size = 0.1
  Size2 = 1
  SupportTransform = false
  UseAllEdges = false
FEATURE [PartDesign::Body] Body002  label="Top frame"
  Group = -> [Sketch004,Pad002,Sketch010,Hole001,Fillet003,Sketch011,Pocket004,Fillet005,Chamfer003]
  Origin = -> Origin002
  Tip = -> Chamfer003
FEATURE [TechDraw::DrawSVGTemplate] Template
  Height = 297
  Orientation = 1
  Width = 420
FEATURE [TechDraw::DrawProjGroupItem] ProjItem  label="Front"
  CoarseView = false
  Direction = (0,0,1)
  Focus = 100
  HardHidden = false
  IsoCount = 0
  IsoHidden = false
  IsoVisible = false
  LockPosition = true
  Perspective = false
  Rotation = 0
  RotationVector = (1,0,0)
  ScaleType = 2
  SeamHidden = false
  SeamVisible = true
  SmoothHidden = false
  SmoothVisible = true
  Source = -> [Body001]
  Type = 0
  X = 0
  XDirection = (1,0,0)
  Y = 0
FEATURE [TechDraw::DrawProjGroup] ProjGroup
  Anchor = -> ProjItem
  AutoDistribute = true
  LockPosition = false
  ProjectionType = 0
  Rotation = 0
  ScaleType = 0
  Source = -> [Body001]
  Views = -> [ProjItem]
  X = 210
  Y = 148.5
  spacingX = 15
  spacingY = 15
FEATURE [TechDraw::DrawViewBalloon] Balloon
  BubbleShape = 1
  EndType = 0
  EndTypeScale = 1
  KinkLength = 5
  LockPosition = false
  OriginX = -13.1
  OriginY = 46.3867
  Rotation = 0
  ScaleType = 0
  ShapeScale = 1
  SourceView = -> ProjItem
  Text = M2 x 2.6mm
  TextWrapLen = -1
  X = -42.0928
  Y = 62.1345
FEATURE [TechDraw::DrawViewBalloon] Balloon001
  BubbleShape = 1
  EndType = 0
  EndTypeScale = 1
  KinkLength = 5
  LockPosition = false
  OriginX = 10.9
  OriginY = 46.3867
  Rotation = 0
  ScaleType = 0
  ShapeScale = 1
  SourceView = -> ProjItem
  Text = M2 x 2.6mm
  TextWrapLen = -1
  X = 41.9927
  Y = 64.5379
FEATURE [TechDraw::DrawViewBalloon] Balloon002
  BubbleShape = 1
  EndType = 0
  EndTypeScale = 1
  KinkLength = 5
  LockPosition = false
  OriginX = -13.1
  OriginY = 22.3867
  Rotation = 0
  ScaleType = 0
  ShapeScale = 1
  SourceView = -> ProjItem
  Text = M2 x 2.6mm
  TextWrapLen = -1
  X = -39.8743
  Y = 13.3608
FEATURE [TechDraw::DrawViewBalloon] Balloon003
  BubbleShape = 1
  EndType = 0
  EndTypeScale = 1
  KinkLength = 5
  LockPosition = false
  OriginX = 10.9
  OriginY = 22.3867
  Rotation = 0
  ScaleType = 0
  ShapeScale = 1
  SourceView = -> ProjItem
  Text = M2 x 2.6mm
  TextWrapLen = -1
  X = 39.0347
  Y = 16.1339
FEATURE [TechDraw::DrawPage] Page  label="Page - Case"
  KeepUpdated = true
  NextBalloonIndex = 5
  ProjectionType = 0
  Template = -> Template
  Views = -> [ProjGroup,Balloon,Balloon001,Balloon002,Balloon003]
FEATURE [TechDraw::DrawSVGTemplate] Template001
  Height = 297
  Orientation = 1
  Width = 420
FEATURE [TechDraw::DrawProjGroupItem] ProjItem001  label="Bottom001"
  CoarseView = false
  Direction = (-2e-16,0,-1)
  Focus = 100
  HardHidden = false
  IsoCount = 0
  IsoHidden = false
  IsoVisible = false
  LockPosition = true
  Perspective = false
  Rotation = 0
  RotationVector = (1,0,0)
  ScaleType = 2
  SeamHidden = false
  SeamVisible = true
  SmoothHidden = false
  SmoothVisible = true
  Source = -> [Body002]
  Type = 0
  X = 0
  XDirection = (-1,0,2e-16)
  Y = 0
FEATURE [TechDraw::DrawProjGroup] ProjGroup001
  Anchor = -> ProjItem001
  AutoDistribute = true
  LockPosition = false
  ProjectionType = 0
  Rotation = 0
  ScaleType = 0
  Source = -> [Body002]
  Views = -> [ProjItem001]
  X = 210
  Y = 148.5
  spacingX = 15
  spacingY = 15
FEATURE [TechDraw::DrawViewBalloon] Balloon004
  BubbleShape = 1
  EndType = 0
  EndTypeScale = 1
  KinkLength = 5
  LockPosition = false
  OriginX = -147.025
  OriginY = 50.675
  Rotation = 0
  ScaleType = 0
  ShapeScale = 1
  SourceView = -> ProjItem001
  Text = M2 x 4.2mm
  TextWrapLen = -1
  X = -112.735
  Y = 80.8822
FEATURE [TechDraw::DrawViewBalloon] Balloon005
  BubbleShape = 1
  EndType = 0
  EndTypeScale = 1
  KinkLength = 5
  LockPosition = false
  OriginX = 144.825
  OriginY = 50.675
  Rotation = 0
  ScaleType = 0
  ShapeScale = 1
  SourceView = -> ProjItem001
  Text = M2 x 4.2mm
  TextWrapLen = -1
  X = 107.665
  Y = 74.4663
FEATURE [TechDraw::DrawViewBalloon] Balloon006
  BubbleShape = 1
  EndType = 0
  EndTypeScale = 1
  KinkLength = 5
  LockPosition = false
  OriginX = -147.025
  OriginY = -50.675
  Rotation = 0
  ScaleType = 0
  ShapeScale = 1
  SourceView = -> ProjItem001
  Text = M2 x 4.2mm
  TextWrapLen = -1
  X = -117.76
  Y = -64.5388
FEATURE [TechDraw::DrawViewBalloon] Balloon007
  BubbleShape = 1
  EndType = 0
  EndTypeScale = 1
  KinkLength = 5
  LockPosition = false
  OriginX = 144.825
  OriginY = -50.675
  Rotation = 0
  ScaleType = 0
  ShapeScale = 1
  SourceView = -> ProjItem001
  Text = M2 x 4.2mm
  TextWrapLen = -1
  X = 119.205
  Y = -64.4111
FEATURE [TechDraw::DrawPage] Page001  label="Page001 - Top frame"
  KeepUpdated = true
  NextBalloonIndex = 5
  ProjectionType = 0
  Template = -> Template001
  Views = -> [ProjGroup001,Balloon004,Balloon005,Balloon006,Balloon007]
